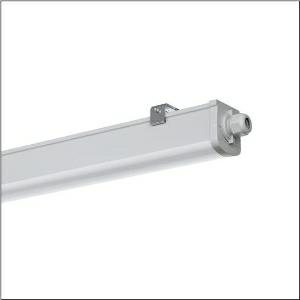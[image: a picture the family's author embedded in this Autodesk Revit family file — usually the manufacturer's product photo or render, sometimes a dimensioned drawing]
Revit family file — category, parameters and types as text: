
# Revit family: monsun_r__31_51fa20dp430b_5f21
name_source: partatom
category: Lighting Fixtures
units: mm (PartAtom-declared; Revit-internal decimal feet)

## family parameters
Cut with Voids When Loaded = No
Host = Face
Light Source = No
Part Type = Normal
Room Calculation Point = No
Round Connector Dimension = Use Diameter
Shared = No

## types (1)
- Monsun® 31 (1 x LED, 3800 lm, 28 W, 4000K)
    Apparent Load = 28 VA
    CIE Flux Codes = 42 72 91 92 100
    Color Rendering = 80
    Color Temperature = 4000K
    Default Elevation = 1800 mm
    Description = Monsun® 31, damp-proof luminaire, primary optical cover: diffuser, of PC, frosted, light emission: direct distribution, primary light characteristic: symmetric, installation type: surface-mounted, LED, rated luminous flux: 3.800lm, luminous efficacy: 136lm/W, light colour: 840, colour temperature: 4000K, control gear: DALI 2, with terminal, 5+1-pole, max. 2.5mm², through-wiring: 3x 2.5mm² + 3x 1.5mm², mains connection: 220..240V, AC, 50/60Hz, rated input power: 28W, housing, luminaire housing, of PC, light grey (RAL 7035), length: 1.458mm, width: 68mm, height: 76mm, protection rating (complete): IP66, insulation class (complete): insulation class II (safety insulation), certification: CE, ENEC, UKCA, protection symbol: D, impact resistance: IK08, permissible operating ambient temperature: -20..+40°C, corresponds to IFS (International Featured Standards) requirements for safety and quality in the food industry, contact your sales advisor before using the luminaires in applications with unclear chemical exposure, large temperature fluctuations or condensation-forming humidity, packaging unit: 1 piece
    Height = 77 mm
    Lamp = 1 x LED
    Lamp Light Flux = 3800 lm
    Lamp Power = 28 W
    Lamp count = 1
    Length = 1518 mm
    Luminous efficacy = 136 lm/W
    Manufacturer = Siteco
    ModVariant = No
    Model = 51FA20DP430B
    Mounting Place = Ceiling
    Mounting Type = Surface mounted
    Number of Poles = 1
    OnlyDefault = Yes
    Power Factor = 1
    Product Name = Monsun® 31
    Product group = damp-proof luminaire
    ProductGroupID = 300
    Protection Class = Protection class II
    Protection Degree = IP 66
    RLX_Detail_Level = 1
    RLX_Emergency_Light_Flux = 0 lm
    RLX_Emergency_Type = 0
    RLX_Emergency_Type_DB = No
    RlxData = <blob elided: 33169 chars, md5=dd812e95>
    Socket = socket
    Standby Power = 0 W
    System Light Flux = 3800 lm
    System Power = 28 W
    Type Comments = Product without accessories
    Type Image = l_1006174.jpg
    URL = http://relux.com
    VarID = ---
    Voltage = 0 V
    Weight = 0.00 kg
    Width = 69 mm

## geometry (parser evidence)
native form markers: Blend x4, Sweep x13
no freeform markers — native parametric forms only
